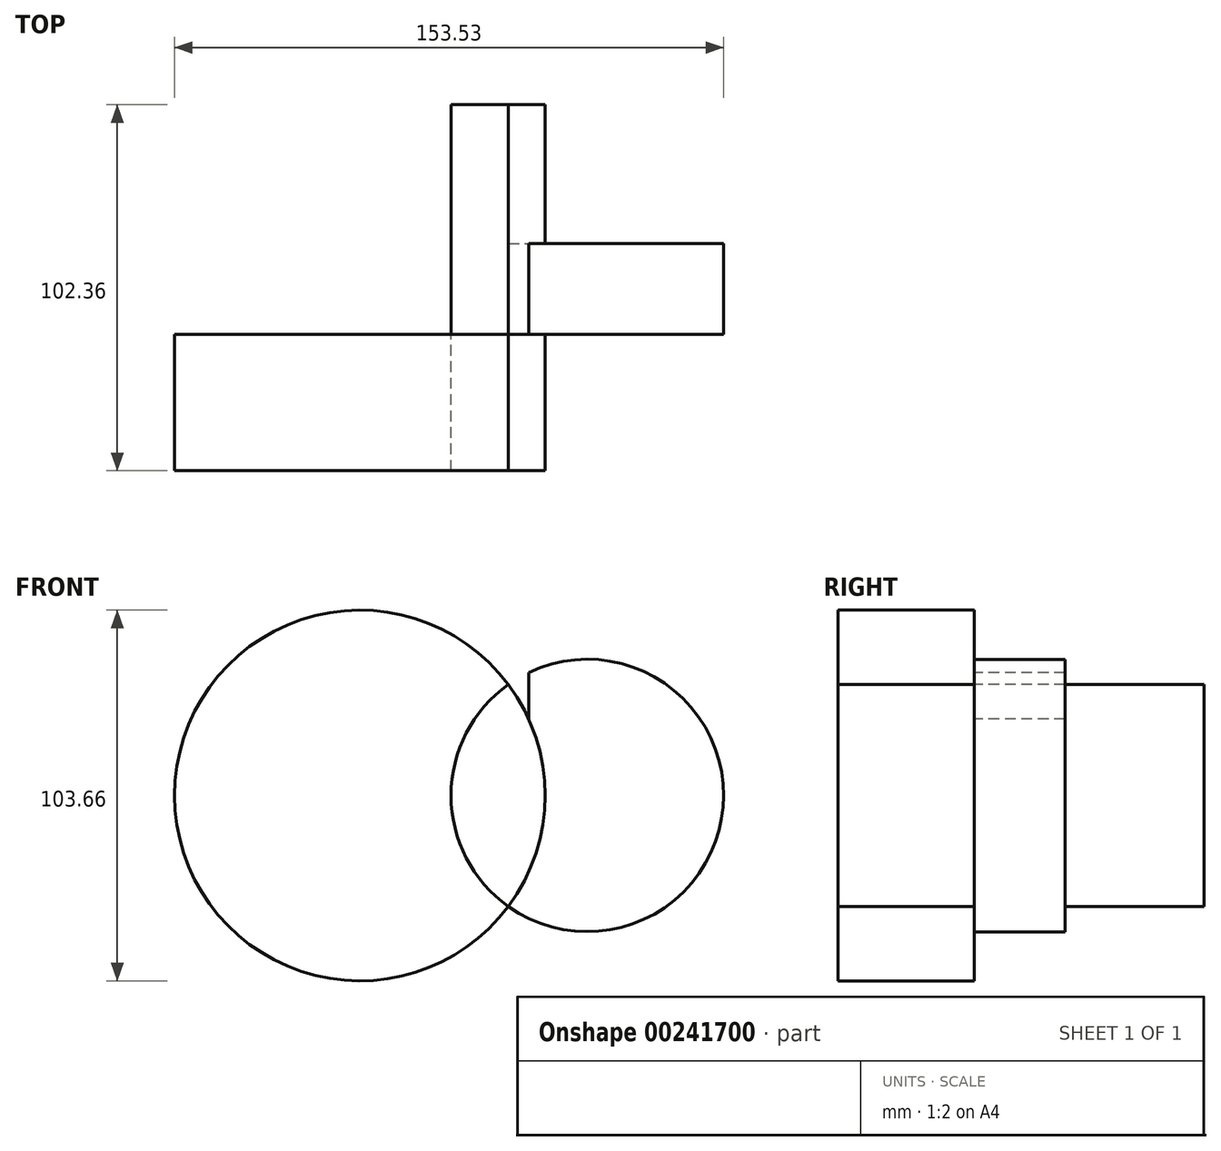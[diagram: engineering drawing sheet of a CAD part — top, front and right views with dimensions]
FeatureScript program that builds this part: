
annotation { "Feature Type Name" : "Feature", "Feature Type Description" : "" }
export const myFeature = defineFeature(function(context is Context, id is Id, definition is map)
    precondition{}
    {
        {
            var Q0;
            Q0=qCreatedBy(makeId("Front.planeOp"),FACE);
            var sketch = newSketch(context, id + "F0", { "sketchPlane" : qUnion([Q0])});
            skCircle(sketch, "E0", {"center": v(0, 0) * mm, "radius": 38.1 * mm});
            skCircle(sketch, "E1", {"center": v(-63.6, 0) * mm, "radius": 51.83 * mm});
            skLineSegment(sketch, "E2", {"start": v(-16.42, 21.46) * mm, "end": v(-16.42, 65.81) * mm});
            skLineSegment(sketch, "E3", {"start": v(-54.52, 51.03) * mm, "end": v(-54.52, 67.29) * mm});
            skLineSegment(sketch, "E4", {"start": v(-54.52, 51.03) * mm, "end": v(-120.38, 31.52) * mm});
            skLineSegment(sketch, "E5", {"start": v(-22.85, -32.02) * mm, "end": v(-101.93, -55.44) * mm});
            skSolve(sketch);
        }
        {
            var Q0;
            {var subQ1=sQuery(id+"F0.wireOp",EDGE,"E1");var subQ3=sQuery(id+"F0.wireOp",EDGE,"E0");var subQ5=makeQuery(id+"F0.imprint","INTERSECT",VERTEX,{"disambiguationData":[OD(0.0)],"derivedFrom":[subQ3,subQ1]});Q0=makeQuery(id+"F0.imprint","IMPRINT",FACE,{"disambiguationData":[TD([[makeQuery(id+"F0.imprint","IMPRINT",EDGE,{"disambiguationData":[TD([[subQ5,-1.0]])],"derivedFrom":subQ3}),-1.0]])]});}
            var Q1;
            {var subQ0=sQuery(id+"F0.wireOp",EDGE,"E5");var subQ1=sQuery(id+"F0.wireOp",EDGE,"E1");var subQ2=makeQuery(id+"F0.imprint","INTERSECT",VERTEX,{"disambiguationData":[OD(0.0)],"derivedFrom":[subQ1,subQ0]});Q1=makeQuery(id+"F0.imprint","IMPRINT",FACE,{"disambiguationData":[TD([[makeQuery(id+"F0.imprint","IMPRINT",EDGE,{"disambiguationData":[TD([[subQ2,1.0]])],"derivedFrom":subQ1}),1.0]])]});}
            var Q2;
            {var subQ0=sQuery(id+"F0.wireOp",EDGE,"E4");var subQ1=sQuery(id+"F0.wireOp",EDGE,"E1");var subQ2=makeQuery(id+"F0.imprint","INTERSECT",VERTEX,{"disambiguationData":[OD(0.0)],"derivedFrom":[subQ1,subQ0]});Q2=makeQuery(id+"F0.imprint","IMPRINT",FACE,{"disambiguationData":[TD([[makeQuery(id+"F0.imprint","IMPRINT",EDGE,{"disambiguationData":[TD([[subQ2,-1.0]])],"derivedFrom":subQ1}),1.0]])]});}
            extrude(context, id + "F1", {"entities" : qUnion([Q0, Q1, Q2]), "depth" : 38.1 * mm});
        }
        {
            var Q0;
            {var subQ0=sQuery(id+"F0.wireOp",EDGE,"E2");var subQ1=sQuery(id+"F0.wireOp",EDGE,"E0");var subQ2=makeQuery(id+"F0.imprint","INTERSECT",VERTEX,{"derivedFrom":[subQ1,subQ0]});Q0=makeQuery(id+"F0.imprint","IMPRINT",FACE,{"disambiguationData":[TD([[makeQuery(id+"F0.imprint","IMPRINT",EDGE,{"disambiguationData":[TD([[subQ2,1.0]])],"derivedFrom":subQ1}),1.0]])]});}
            extrude(context, id + "F2", {"entities" : qUnion([Q0]), "oppositeDirection" : true, "depth" : 25.4 * mm});
        }
        {
            var Q0;
            {var subQ0=sQuery(id+"F0.wireOp",EDGE,"E1");var subQ1=sQuery(id+"F0.wireOp",EDGE,"E0");var subQ2=makeQuery(id+"F0.imprint","INTERSECT",VERTEX,{"disambiguationData":[OD(0.0)],"derivedFrom":[subQ1,subQ0]});Q0=makeQuery(id+"F0.imprint","IMPRINT",FACE,{"disambiguationData":[TD([[makeQuery(id+"F0.imprint","IMPRINT",EDGE,{"disambiguationData":[TD([[subQ2,-1.0]])],"derivedFrom":subQ1}),1.0]])]});}
            extrude(context, id + "F3", {"entities" : qUnion([Q0]), "operationType" : NewBodyOperationType.ADD, "oppositeDirection" : true, "depth" : 64.26 * mm});
        }
        {
            var Q0;
            {var subQ0=sQuery(id+"F0.wireOp",EDGE,"E1");var subQ1=sQuery(id+"F0.wireOp",EDGE,"E0");var subQ2=makeQuery(id+"F0.imprint","INTERSECT",VERTEX,{"disambiguationData":[OD(0.0)],"derivedFrom":[subQ1,subQ0]});Q0=makeQuery(id+"F0.imprint","IMPRINT",FACE,{"disambiguationData":[TD([[makeQuery(id+"F0.imprint","IMPRINT",EDGE,{"disambiguationData":[TD([[subQ2,-1.0]])],"derivedFrom":subQ1}),1.0]])]});}
            extrude(context, id + "F4", {"entities" : qUnion([Q0]), "depth" : 38.1 * mm});
        }
    });
